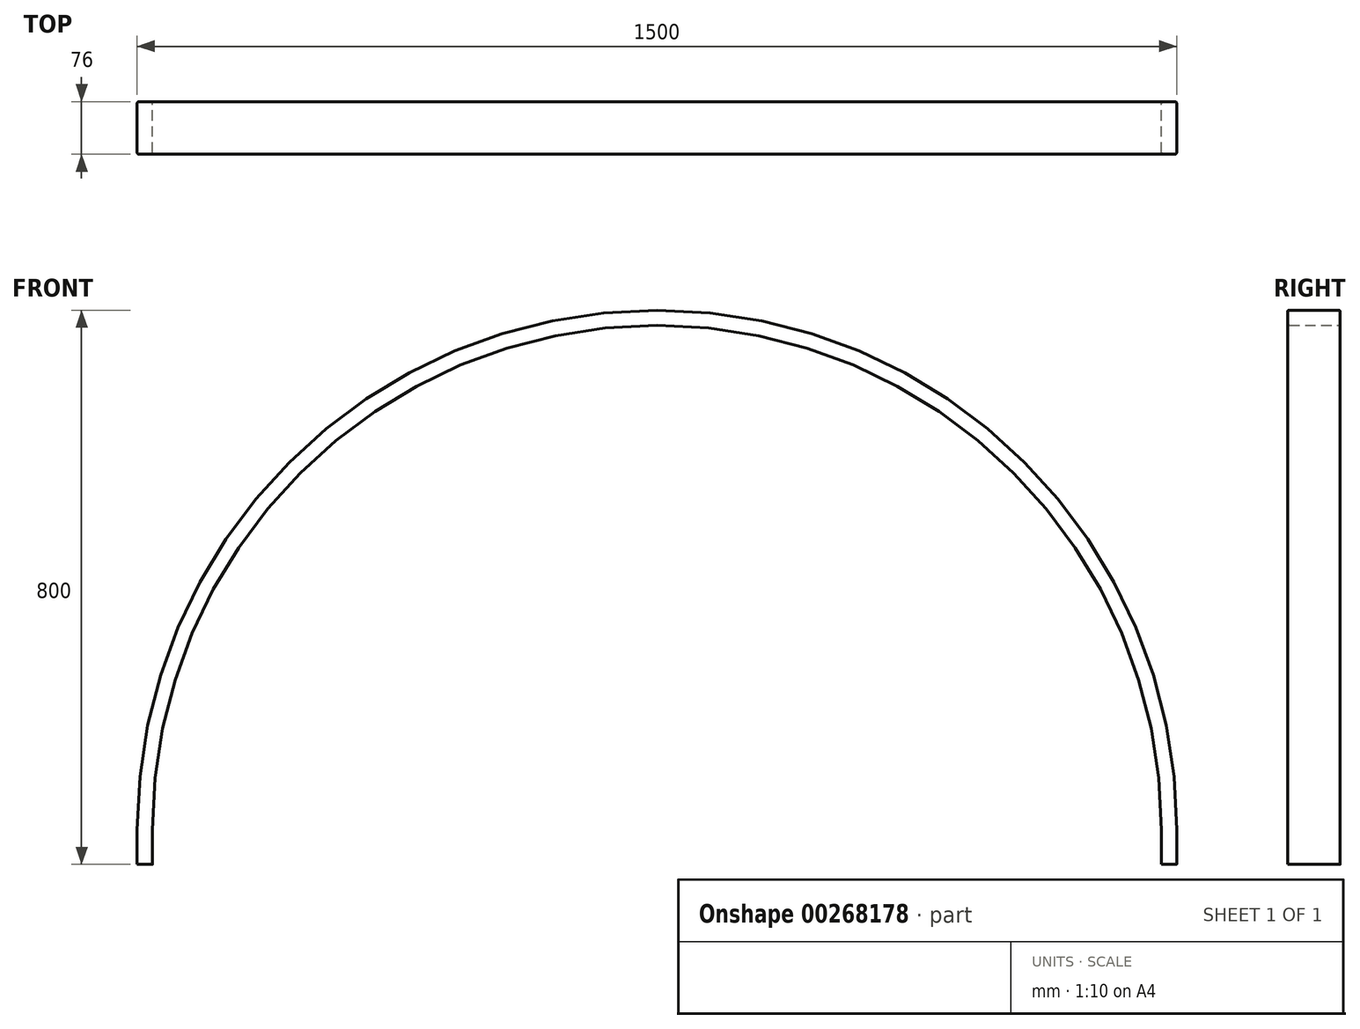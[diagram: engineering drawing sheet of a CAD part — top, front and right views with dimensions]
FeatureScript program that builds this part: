
annotation { "Feature Type Name" : "Feature", "Feature Type Description" : "" }
export const myFeature = defineFeature(function(context is Context, id is Id, definition is map)
    precondition{}
    {
        {
            var Q0;
            Q0=qCreatedBy(makeId("Front.planeOp"),FACE);
            var sketch = newSketch(context, id + "F0", { "sketchPlane" : qUnion([Q0])});
            skLineSegment(sketch, "E0.top", {"start": v(900, 1050) * mm, "end": v(878, 1050) * mm});
            skPoint(sketch, "E0.middle", {"position": v(0, 0) * mm});
            skArc(sketch, "E1", {"start": v(900, 1050) * mm, "mid": v(150, 1800) * mm, "end": v(-600, 1050) * mm});
            skArc(sketch, "E2.0", {"start": v(878, 1050) * mm, "mid": v(150, 1778) * mm, "end": v(-578, 1050) * mm});
            skLineSegment(sketch, "E3.trimOffspring", {"start": v(-578, 1050) * mm, "end": v(-600, 1050) * mm});
            skLineSegment(sketch, "E4", {"start": v(-600, 1050) * mm, "end": v(-600, 1000) * mm});
            skLineSegment(sketch, "E5", {"start": v(-600, 1000) * mm, "end": v(-578, 1000) * mm});
            skLineSegment(sketch, "E6", {"start": v(-578, 1000) * mm, "end": v(-578, 1050) * mm});
            skLineSegment(sketch, "E7", {"start": v(878, 1050) * mm, "end": v(878, 1000) * mm});
            skLineSegment(sketch, "E8", {"start": v(878, 1000) * mm, "end": v(900, 1000) * mm});
            skLineSegment(sketch, "E9", {"start": v(900, 1000) * mm, "end": v(900, 1050) * mm});
            skSolve(sketch);
        }
        {
            var Q0;
            Q0=makeQuery(id+"F0.imprint","IMPRINT",FACE,{"disambiguationData":[TD([[makeQuery(id+"F0.imprint","IMPRINT",EDGE,{"derivedFrom":sQuery(id+"F0.wireOp",EDGE,"E0.top")}),-1.0]])]});
            var Q1;
            Q1=makeQuery(id+"F0.imprint","IMPRINT",FACE,{"disambiguationData":[TD([[makeQuery(id+"F0.imprint","IMPRINT",EDGE,{"derivedFrom":sQuery(id+"F0.wireOp",EDGE,"E3.trimOffspring")}),1.0]])]});
            var Q2;
            Q2=makeQuery(id+"F0.imprint","IMPRINT",FACE,{"disambiguationData":[TD([[makeQuery(id+"F0.imprint","IMPRINT",EDGE,{"derivedFrom":sQuery(id+"F0.wireOp",EDGE,"E0.top")}),1.0]])]});
            extrude(context, id + "F1", {"entities" : qUnion([Q0, Q1, Q2]), "depth" : 76 * mm});
        }
        {
            var Q0;
            Q0=makeQuery(id+"F1.opExtrude","CAP_EDGE",EDGE,{"disambiguationData":[OSD([sQuery(id+"F0.wireOp",EDGE,"E1")])],"isStart":true});
            var Q1;
            Q1=makeQuery(id+"F1.opExtrude","CAP_EDGE",EDGE,{"disambiguationData":[OSD([sQuery(id+"F0.wireOp",EDGE,"E1")])],"isStart":false});
            var Q2;
            Q2=makeQuery(id+"F1.opExtrude","CAP_EDGE",EDGE,{"disambiguationData":[OSD([sQuery(id+"F0.wireOp",EDGE,"E2.0")])],"isStart":false});
            var Q3;
            Q3=makeQuery(id+"F1.opExtrude","CAP_EDGE",EDGE,{"disambiguationData":[OSD([sQuery(id+"F0.wireOp",EDGE,"E2.0")])],"isStart":true});
            fillet(context, id + "F2", {"entities" : qUnion([Q0, Q1, Q2, Q3]), "radius" : 2.5 * mm, "tangentPropagation" : true, "allowEdgeOverflow" : false});
        }
    });
